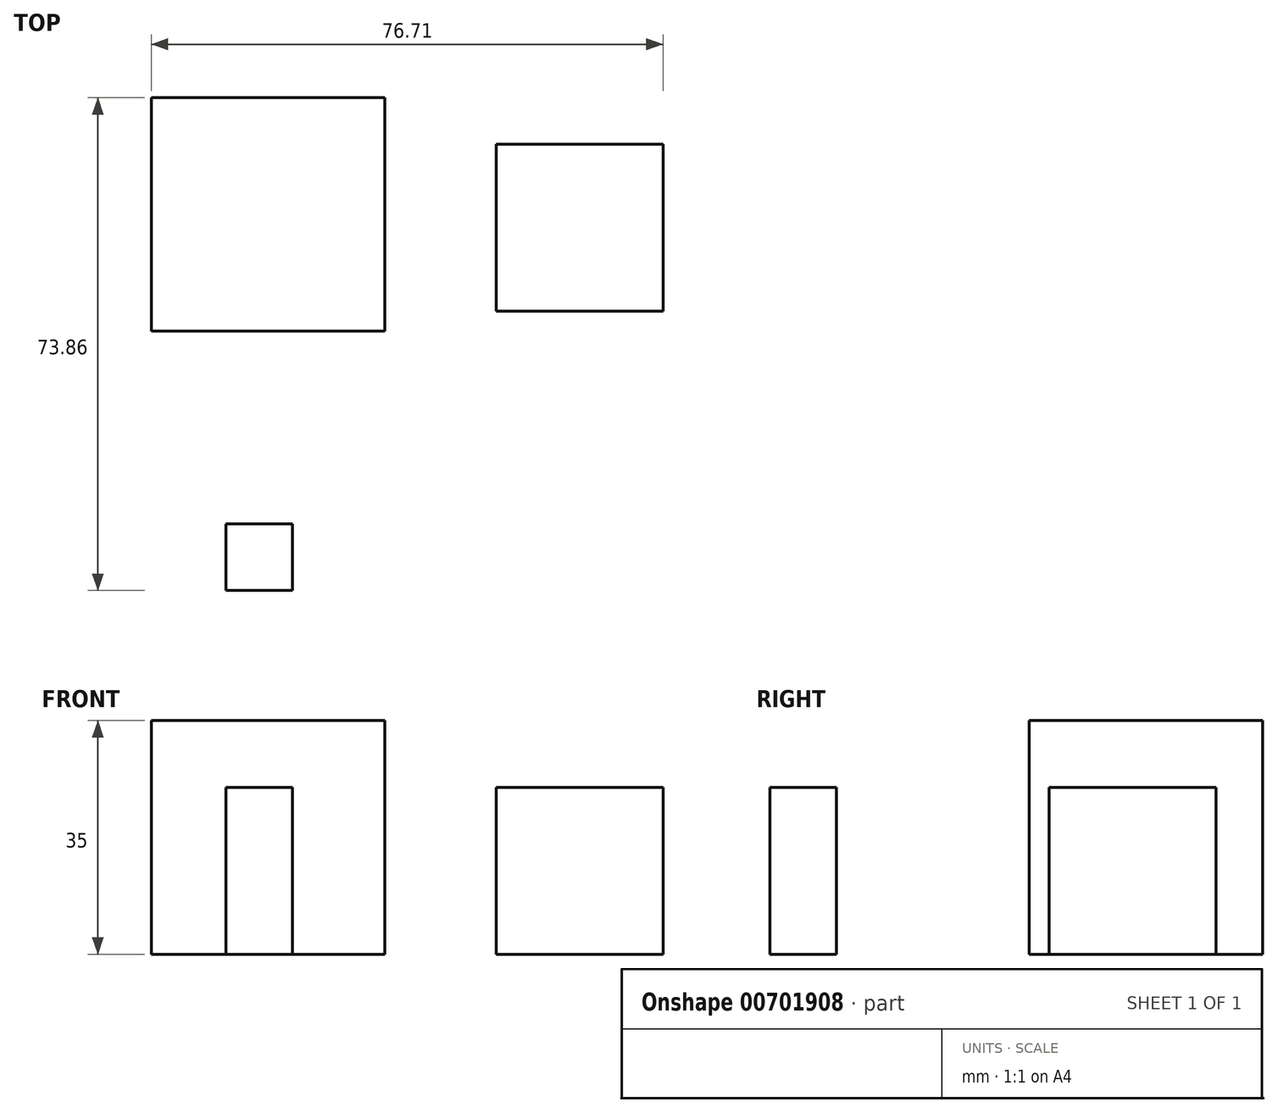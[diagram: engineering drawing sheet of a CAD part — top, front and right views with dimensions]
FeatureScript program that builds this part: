
annotation { "Feature Type Name" : "Feature", "Feature Type Description" : "" }
export const myFeature = defineFeature(function(context is Context, id is Id, definition is map)
    precondition{}
    {
        {
            var Q0;
            Q0=qCreatedBy(makeId("Top.planeOp"),FACE);
            var sketch = newSketch(context, id + "F0", { "sketchPlane" : qUnion([Q0])});
            skLineSegment(sketch, "E0.bottom", {"start": v(-10.27, 14.56) * mm, "end": v(14.73, 14.56) * mm});
            skLineSegment(sketch, "E0.top", {"start": v(-10.27, -10.44) * mm, "end": v(14.73, -10.44) * mm});
            skLineSegment(sketch, "E0.left", {"start": v(-10.27, 14.56) * mm, "end": v(-10.27, -10.44) * mm});
            skLineSegment(sketch, "E0.right", {"start": v(14.73, 14.56) * mm, "end": v(14.73, -10.44) * mm});
            skSolve(sketch);
        }
        {
            var Q0;
            Q0 = qSketchRegion(id + "F0", true);
            extrude(context, id + "F1", {"entities" : qUnion([Q0]), "depth" : 25 * mm, "offsetDistance" : 25 * mm});
        }
        {
            var Q0;
            Q0=qCreatedBy(makeId("Top.planeOp"),FACE);
            var sketch = newSketch(context, id + "F2", { "sketchPlane" : qUnion([Q0])});
            skLineSegment(sketch, "E1.bottom", {"start": v(-61.98, 21.56) * mm, "end": v(-26.98, 21.56) * mm});
            skLineSegment(sketch, "E1.top", {"start": v(-61.98, -13.44) * mm, "end": v(-26.98, -13.44) * mm});
            skLineSegment(sketch, "E1.left", {"start": v(-61.98, 21.56) * mm, "end": v(-61.98, -13.44) * mm});
            skLineSegment(sketch, "E1.right", {"start": v(-26.98, 21.56) * mm, "end": v(-26.98, -13.44) * mm});
            skSolve(sketch);
        }
        {
            var Q0;
            Q0=makeQuery(id+"F2.imprint","IMPRINT",FACE,{"disambiguationData":[TD([[makeQuery(id+"F2.imprint","IMPRINT",EDGE,{"derivedFrom":sQuery(id+"F2.wireOp",EDGE,"E1.bottom")}),-1.0]])]});
            extrude(context, id + "F3", {"entities" : qUnion([Q0]), "depth" : 35 * mm, "offsetDistance" : 25 * mm});
        }
        {
            var Q0;
            Q0=qCreatedBy(makeId("Top.planeOp"),FACE);
            var sketch = newSketch(context, id + "F4", { "sketchPlane" : qUnion([Q0])});
            skLineSegment(sketch, "E2.bottom", {"start": v(-50.8, -42.3) * mm, "end": v(-40.8, -42.3) * mm});
            skLineSegment(sketch, "E2.top", {"start": v(-50.8, -52.3) * mm, "end": v(-40.8, -52.3) * mm});
            skLineSegment(sketch, "E2.left", {"start": v(-50.8, -42.3) * mm, "end": v(-50.8, -52.3) * mm});
            skLineSegment(sketch, "E2.right", {"start": v(-40.8, -42.3) * mm, "end": v(-40.8, -52.3) * mm});
            skSolve(sketch);
        }
        {
            var Q0;
            Q0=makeQuery(id+"F4.imprint","IMPRINT",FACE,{"disambiguationData":[TD([[makeQuery(id+"F4.imprint","IMPRINT",EDGE,{"derivedFrom":sQuery(id+"F4.wireOp",EDGE,"E2.bottom")}),-1.0]])]});
            extrude(context, id + "F5", {"entities" : qUnion([Q0]), "depth" : 25 * mm, "offsetDistance" : 25 * mm});
        }
    });
